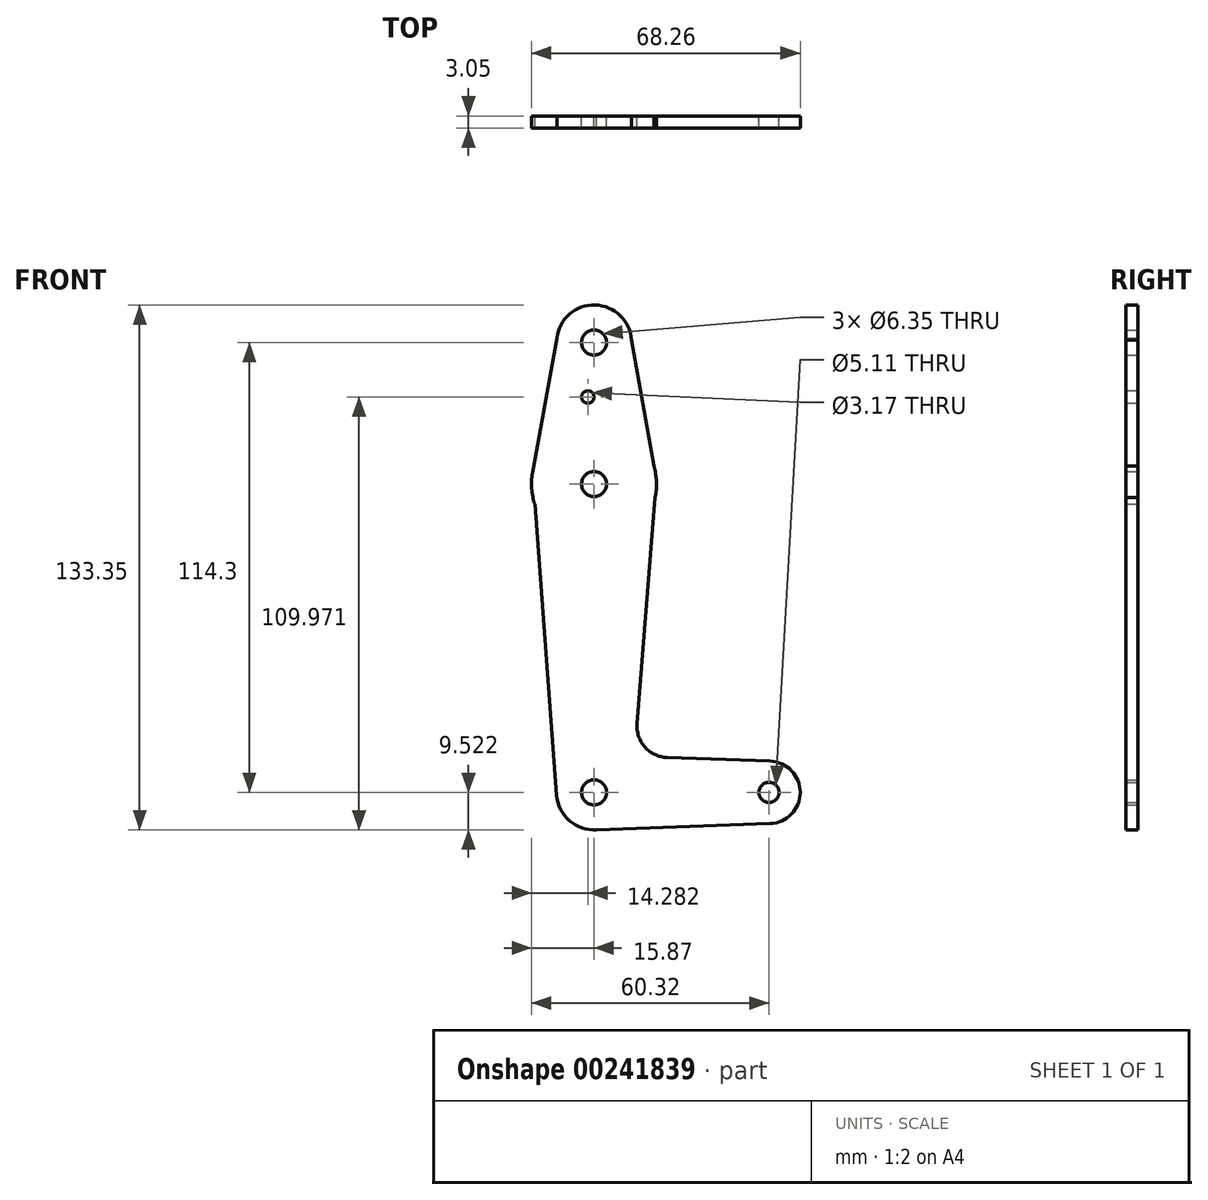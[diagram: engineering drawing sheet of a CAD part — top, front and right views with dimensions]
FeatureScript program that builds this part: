
annotation { "Feature Type Name" : "Feature", "Feature Type Description" : "" }
export const myFeature = defineFeature(function(context is Context, id is Id, definition is map)
    precondition{}
    {
        {
            var Q0;
            Q0=qCreatedBy(makeId("Front.planeOp"),FACE);
            var sketch = newSketch(context, id + "F0", { "sketchPlane" : qUnion([Q0])});
            skLineSegment(sketch, "E0", {"start": v(0, 85.6) * mm, "end": v(0, -28.7) * mm});
            skLineSegment(sketch, "E1", {"start": v(0, -28.7) * mm, "end": v(44.45, -28.7) * mm});
            skCircle(sketch, "E2", {"center": v(0, 85.6) * mm, "radius": 9.53 * mm});
            skCircle(sketch, "E3", {"center": v(0, 49.64) * mm, "radius": 15.88 * mm});
            skCircle(sketch, "E4", {"center": v(0, -28.7) * mm, "radius": 9.53 * mm});
            skCircle(sketch, "E5", {"center": v(44.45, -28.7) * mm, "radius": 7.94 * mm});
            skLineSegment(sketch, "E6", {"start": v(-9.46, 86.7) * mm, "end": v(-15.62, 52.45) * mm});
            skLineSegment(sketch, "E7", {"start": v(9.5, 86.21) * mm, "end": v(15.85, 50.58) * mm});
            skLineSegment(sketch, "E8", {"start": v(-15.62, 52.45) * mm, "end": v(-9.5, -29.4) * mm});
            skLineSegment(sketch, "E9", {"start": v(15.85, 50.58) * mm, "end": v(10.94, -11.26) * mm});
            skLineSegment(sketch, "E10", {"start": v(0, -38.22) * mm, "end": v(44.73, -36.63) * mm});
            skLineSegment(sketch, "E11", {"start": v(18.58, -19.83) * mm, "end": v(44.73, -20.77) * mm});
            skCircle(sketch, "E12", {"center": v(0, 85.6) * mm, "radius": 3.18 * mm});
            skCircle(sketch, "E13", {"center": v(0, 49.64) * mm, "radius": 3.18 * mm});
            skCircle(sketch, "E14", {"center": v(0, -28.7) * mm, "radius": 3.18 * mm});
            skCircle(sketch, "E15", {"center": v(44.45, -28.7) * mm, "radius": 2.55 * mm});
            skCircle(sketch, "E16", {"center": v(-1.59, 71.75) * mm, "radius": 1.59 * mm});
            skArc(sketch, "E17.filletArc", {"start": v(10.94, -11.26) * mm, "mid": v(12.93, -17.18) * mm, "end": v(18.58, -19.83) * mm});
            skSolve(sketch);
        }
        {
            var Q0;
            Q0 = qSketchRegion(id + "F0", true);
            var Q1;
            {var subQ0=sQuery(id+"F0.wireOp",EDGE,"E4");var subQ1=sQuery(id+"F0.wireOp",EDGE,"E0");var subQ2=makeQuery(id+"F0.imprint","INTERSECT",VERTEX,{"derivedFrom":[subQ1,subQ0]});Q1=makeQuery(id+"F0.imprint","IMPRINT",FACE,{"disambiguationData":[TD([[makeQuery(id+"F0.imprint","IMPRINT",EDGE,{"disambiguationData":[TD([[subQ2,-1.0]])],"derivedFrom":subQ1}),1.0]])]});}
            extrude(context, id + "F1", {"entities" : qUnion([Q0, Q1]), "depth" : 3.05 * mm});
        }
    });
